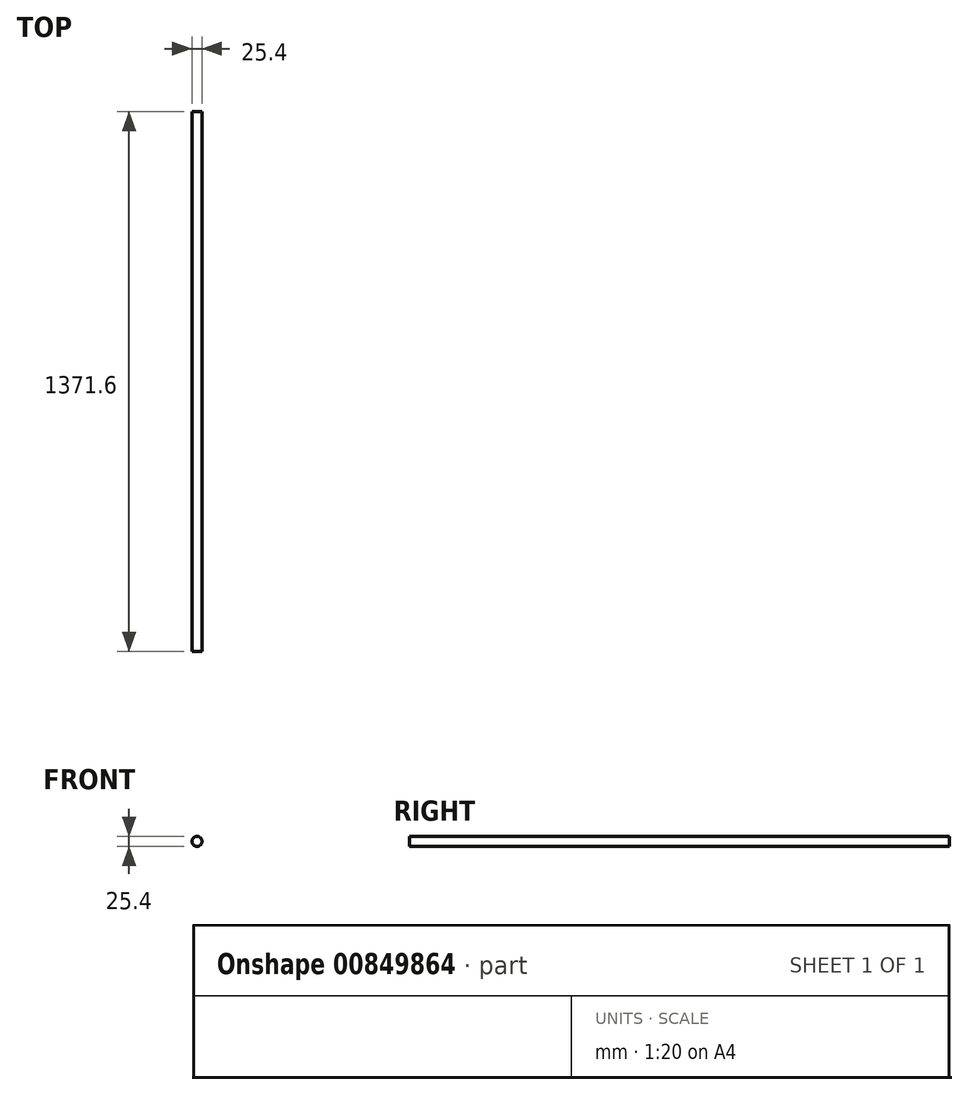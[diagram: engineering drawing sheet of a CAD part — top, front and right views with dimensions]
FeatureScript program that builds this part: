
annotation { "Feature Type Name" : "Feature", "Feature Type Description" : "" }
export const myFeature = defineFeature(function(context is Context, id is Id, definition is map)
    precondition{}
    {
        {
            var Q0;
            Q0=qCreatedBy(makeId("Front.planeOp"),FACE);
            var sketch = newSketch(context, id + "F0", { "sketchPlane" : qUnion([Q0])});
            skCircle(sketch, "E0", {"center": v(0, 0) * mm, "radius": 12.7 * mm});
            skSolve(sketch);
        }
        {
            var Q0;
            Q0=makeQuery(id+"F0.imprint","IMPRINT",FACE,{"disambiguationData":[TD([[makeQuery(id+"F0.imprint","IMPRINT",EDGE,{"derivedFrom":sQuery(id+"F0.wireOp",EDGE,"E0")}),1.0]])]});
            extrude(context, id + "F1", {"entities" : qUnion([Q0]), "oppositeDirection" : true, "depth" : 1371.6 * mm, "offsetDistance" : 25.4 * mm});
        }
        {
            var Q0;
            Q0=makeQuery(id+"F1.opExtrude","CAP_FACE",FACE,{"disambiguationData":[OSD([sQuery(id+"F0.wireOp",EDGE,"E0")])],"isStart":false});
            var sketch = newSketch(context, id + "F2", { "sketchPlane" : qUnion([Q0])});
            skLineSegment(sketch, "E1", {"start": v(0, 0) * mm, "end": v(0, -12.7) * mm});
            skLineSegment(sketch, "E2", {"start": v(0, 0) * mm, "end": v(0, 12.7) * mm});
            skLineSegment(sketch, "E3", {"start": v(0, 0) * mm, "end": v(-12.7, 0) * mm});
            skLineSegment(sketch, "E4", {"start": v(0, 0) * mm, "end": v(12.7, 0) * mm});
            skPoint(sketch, "E5", {"position": v(0, 12.7) * mm});
            skPoint(sketch, "E6", {"position": v(12.7, 0) * mm});
            skPoint(sketch, "E7", {"position": v(-12.7, 0) * mm});
            skPoint(sketch, "E8", {"position": v(0, -12.7) * mm});
            skSolve(sketch);
        }
        {
            var Q0;
            Q0=qCreatedBy(makeId("Top.planeOp"),FACE);
            cPlane(context, id + "F3", {"entities" : qUnion([Q0]), "cplaneType" : CPlaneType.OFFSET, "offset" : 12.7 * mm, "width" : 152.4 * mm, "height" : 152.4 * mm});
        }
    });
